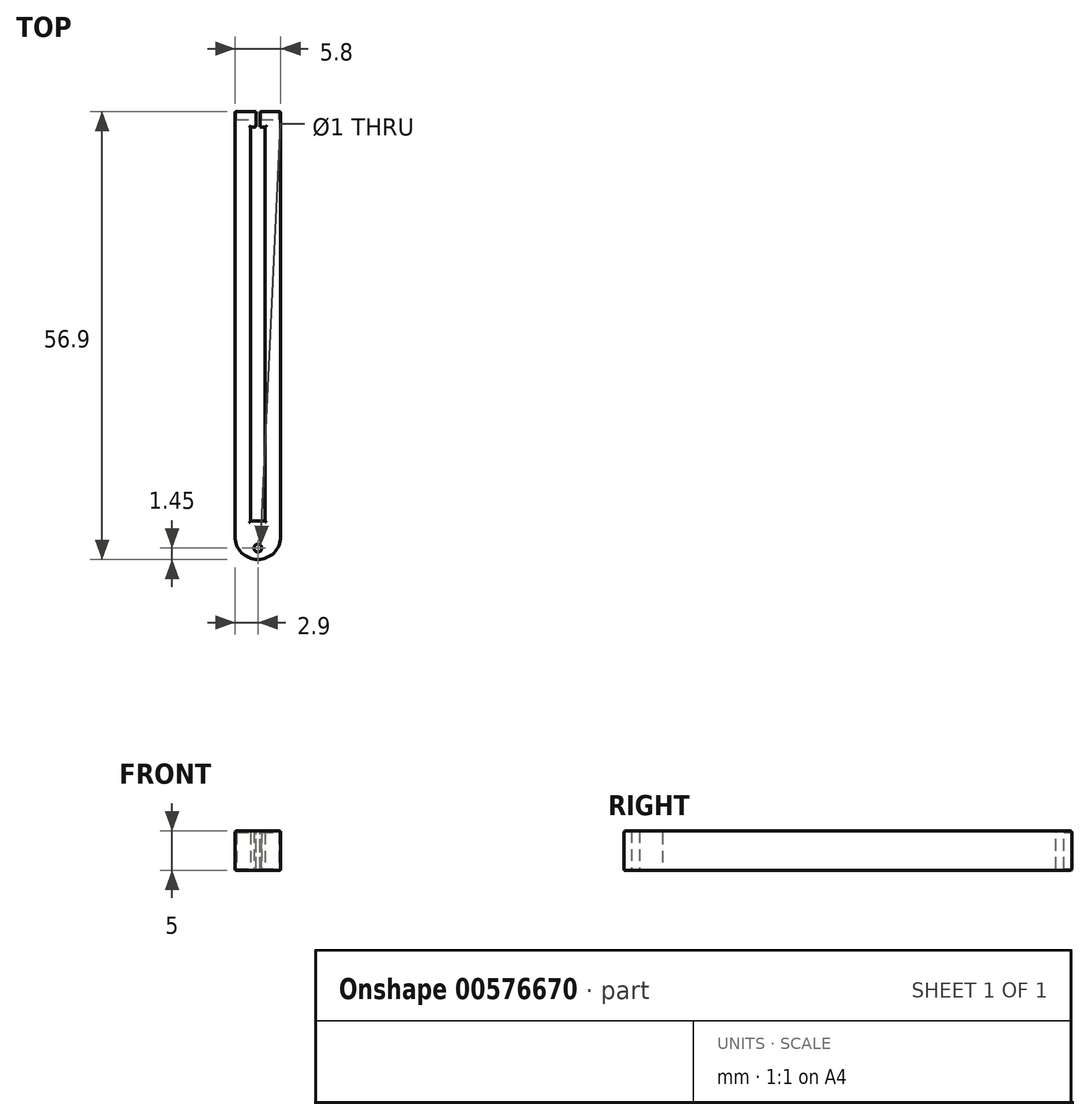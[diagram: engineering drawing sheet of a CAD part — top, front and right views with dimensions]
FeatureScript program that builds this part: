
annotation { "Feature Type Name" : "Feature", "Feature Type Description" : "" }
export const myFeature = defineFeature(function(context is Context, id is Id, definition is map)
    precondition{}
    {
        {
            var Q0;
            Q0=qCreatedBy(makeId("Top.planeOp"),FACE);
            var sketch = newSketch(context, id + "F0", { "sketchPlane" : qUnion([Q0])});
            skLineSegment(sketch, "E0", {"start": v(0, 0) * mm, "end": v(0, 50) * mm});
            skLineSegment(sketch, "E1", {"start": v(0, 50) * mm, "end": v(-1.8, 50) * mm});
            skLineSegment(sketch, "E2", {"start": v(-1.8, 50) * mm, "end": v(-1.8, 0) * mm});
            skLineSegment(sketch, "E3", {"start": v(-1.8, 0) * mm, "end": v(0, 0) * mm});
            skLineSegment(sketch, "E4", {"start": v(2, 52) * mm, "end": v(2, -2) * mm});
            skLineSegment(sketch, "E5", {"start": v(2, -2) * mm, "end": v(-3.8, -2) * mm});
            skLineSegment(sketch, "E6", {"start": v(-3.8, -2) * mm, "end": v(-3.8, 52) * mm});
            skLineSegment(sketch, "E7", {"start": v(-3.8, 52) * mm, "end": v(2, 52) * mm});
            skLineSegment(sketch, "E8", {"start": v(-0.9, -2) * mm, "end": v(-0.9, -4.9) * mm});
            skArc(sketch, "E9", {"start": v(-3.8, -2) * mm, "mid": v(-0.9, -4.9) * mm, "end": v(2, -2) * mm});
            skCircle(sketch, "E10", {"center": v(-0.9, -3.45) * mm, "radius": 0.5 * mm});
            skSolve(sketch);
        }
        {
            var Q0;
            Q0=makeQuery(id+"F0.imprint","IMPRINT",FACE,{"disambiguationData":[TD([[makeQuery(id+"F0.imprint","IMPRINT",EDGE,{"derivedFrom":sQuery(id+"F0.wireOp",EDGE,"E0")}),-1.0]])]});
            var Q1;
            {var subQ1=sQuery(id+"F0.wireOp",EDGE,"E5");var subQ3=sQuery(id+"F0.wireOp",EDGE,"E8");var subQ7=makeQuery(id+"F0.imprint","INTERSECT",VERTEX,{"derivedFrom":[subQ1,subQ3]});Q1=makeQuery(id+"F0.imprint","IMPRINT",FACE,{"disambiguationData":[TD([[makeQuery(id+"F0.imprint","IMPRINT",EDGE,{"disambiguationData":[TD([[subQ7,-1.0]])],"derivedFrom":subQ3}),1.0]])]});}
            var Q2;
            {var subQ1=sQuery(id+"F0.wireOp",EDGE,"E5");var subQ3=sQuery(id+"F0.wireOp",EDGE,"E8");var subQ5=makeQuery(id+"F0.imprint","INTERSECT",VERTEX,{"derivedFrom":[subQ1,subQ3]});Q2=makeQuery(id+"F0.imprint","IMPRINT",FACE,{"disambiguationData":[TD([[makeQuery(id+"F0.imprint","IMPRINT",EDGE,{"disambiguationData":[TD([[subQ5,-1.0]])],"derivedFrom":subQ3}),-1.0]])]});}
            extrude(context, id + "F1", {"entities" : qUnion([Q0, Q1, Q2]), "depth" : 5 * mm, "offsetDistance" : 25 * mm});
        }
        {
            var Q0;
            Q0=makeQuery(id+"F1.opExtrude","SWEPT_FACE",FACE,{"disambiguationData":[OSD([sQuery(id+"F0.wireOp",EDGE,"E7")])]});
            var sketch = newSketch(context, id + "F2", { "sketchPlane" : qUnion([Q0])});
            skLineSegment(sketch, "E11", {"start": v(0.65, 0) * mm, "end": v(0.65, 5) * mm});
            skLineSegment(sketch, "E12", {"start": v(1.15, 0) * mm, "end": v(1.15, 5) * mm});
            skLineSegment(sketch, "E13", {"start": v(1.15, 5) * mm, "end": v(0.65, 5) * mm});
            skLineSegment(sketch, "E14", {"start": v(1.15, 0) * mm, "end": v(0.65, 0) * mm});
            skSolve(sketch);
        }
        {
            var Q0;
            Q0=makeQuery(id+"F2.imprint","IMPRINT",FACE,{"disambiguationData":[TD([[makeQuery(id+"F2.imprint","IMPRINT",EDGE,{"derivedFrom":sQuery(id+"F2.wireOp",EDGE,"E11")}),-1.0]])]});
            extrude(context, id + "F3", {"entities" : qUnion([Q0]), "operationType" : NewBodyOperationType.REMOVE, "oppositeDirection" : true, "depth" : 2 * mm, "offsetDistance" : 25 * mm});
        }
        {
            var Q0;
            Q0=makeQuery(id+"F1.opExtrude","SWEPT_EDGE",EDGE,{"disambiguationData":[OSD([sQuery(id+"F0.wireOp",EDGE,"E4"),sQuery(id+"F0.wireOp",EDGE,"E7")])]});
            var Q1;
            {var subQ0=sQuery(id+"F0.wireOp",EDGE,"E7");var subQ1=sQuery(id+"F0.wireOp",EDGE,"E4");Q1=makeQuery(id+"F3.boolean.opBoolean","SPLIT",EDGE,{"disambiguationData":[TD([makeQuery(id+"F1.opExtrude","SWEPT_FACE",FACE,{"disambiguationData":[OSD([subQ1])]})])],"derivedFrom":makeQuery(id+"F1.opExtrude","CAP_EDGE",EDGE,{"disambiguationData":[OSD([subQ0])],"isStart":true})});}
            var Q2;
            {var subQ0=sQuery(id+"F0.wireOp",EDGE,"E7");var subQ1=sQuery(id+"F0.wireOp",EDGE,"E4");Q2=makeQuery(id+"F3.boolean.opBoolean","SPLIT",EDGE,{"disambiguationData":[TD([makeQuery(id+"F1.opExtrude","SWEPT_FACE",FACE,{"disambiguationData":[OSD([subQ1])]})])],"derivedFrom":makeQuery(id+"F1.opExtrude","CAP_EDGE",EDGE,{"disambiguationData":[OSD([subQ0])],"isStart":false})});}
            var Q3;
            {var subQ0=sQuery(id+"F0.wireOp",EDGE,"E7");var subQ1=sQuery(id+"F0.wireOp",EDGE,"E6");Q3=makeQuery(id+"F3.boolean.opBoolean","SPLIT",EDGE,{"disambiguationData":[TD([makeQuery(id+"F1.opExtrude","SWEPT_FACE",FACE,{"disambiguationData":[OSD([subQ1])]})])],"derivedFrom":makeQuery(id+"F1.opExtrude","CAP_EDGE",EDGE,{"disambiguationData":[OSD([subQ0])],"isStart":false})});}
            var Q4;
            Q4=makeQuery(id+"F1.opExtrude","SWEPT_EDGE",EDGE,{"disambiguationData":[OSD([sQuery(id+"F0.wireOp",EDGE,"E6"),sQuery(id+"F0.wireOp",EDGE,"E7")])]});
            var Q5;
            {var subQ0=sQuery(id+"F0.wireOp",EDGE,"E7");var subQ1=sQuery(id+"F0.wireOp",EDGE,"E6");Q5=makeQuery(id+"F3.boolean.opBoolean","SPLIT",EDGE,{"disambiguationData":[TD([makeQuery(id+"F1.opExtrude","SWEPT_FACE",FACE,{"disambiguationData":[OSD([subQ1])]})])],"derivedFrom":makeQuery(id+"F1.opExtrude","CAP_EDGE",EDGE,{"disambiguationData":[OSD([subQ0])],"isStart":true})});}
            var Q6;
            Q6=makeQuery(id+"F3.boolean.opBoolean","COPY",EDGE,{"derivedFrom":makeQuery(id+"F3.opExtrude","CAP_EDGE",EDGE,{"disambiguationData":[OSD([sQuery(id+"F2.wireOp",EDGE,"E11")])],"isStart":true})});
            var Q7;
            Q7=makeQuery(id+"F3.boolean.opBoolean","COPY",EDGE,{"derivedFrom":makeQuery(id+"F3.opExtrude","CAP_EDGE",EDGE,{"disambiguationData":[OSD([sQuery(id+"F2.wireOp",EDGE,"E12")])],"isStart":true})});
            var Q8;
            Q8=makeQuery(id+"F3.boolean.opBoolean","COPY",EDGE,{"derivedFrom":makeQuery(id+"F3.opExtrude","SWEPT_EDGE",EDGE,{"disambiguationData":[OSD([sQuery(id+"F0.wireOp",EDGE,"E7"),sQuery(id+"F2.wireOp",EDGE,"E12"),sQuery(id+"F2.wireOp",EDGE,"E13")])]})});
            var Q9;
            Q9=makeQuery(id+"F3.boolean.opBoolean","COPY",EDGE,{"derivedFrom":makeQuery(id+"F3.opExtrude","SWEPT_EDGE",EDGE,{"disambiguationData":[OSD([sQuery(id+"F0.wireOp",EDGE,"E7"),sQuery(id+"F2.wireOp",EDGE,"E11"),sQuery(id+"F2.wireOp",EDGE,"E13")])]})});
            var Q10;
            Q10=makeQuery(id+"F3.boolean.opBoolean","COPY",EDGE,{"derivedFrom":makeQuery(id+"F3.opExtrude","SWEPT_EDGE",EDGE,{"disambiguationData":[OSD([sQuery(id+"F0.wireOp",EDGE,"E7"),sQuery(id+"F2.wireOp",EDGE,"E11"),sQuery(id+"F2.wireOp",EDGE,"E14")])]})});
            var Q11;
            Q11=makeQuery(id+"F3.boolean.opBoolean","COPY",EDGE,{"derivedFrom":makeQuery(id+"F3.opExtrude","SWEPT_EDGE",EDGE,{"disambiguationData":[OSD([sQuery(id+"F0.wireOp",EDGE,"E7"),sQuery(id+"F2.wireOp",EDGE,"E12"),sQuery(id+"F2.wireOp",EDGE,"E14")])]})});
            var Q12;
            {var subQ0=sQuery(id+"F0.wireOp",EDGE,"E2");var subQ1=sQuery(id+"F0.wireOp",EDGE,"E1");Q12=makeQuery(id+"F3.boolean.opBoolean","SPLIT",EDGE,{"disambiguationData":[TD([makeQuery(id+"F1.opExtrude","SWEPT_FACE",FACE,{"disambiguationData":[OSD([subQ0])]})])],"derivedFrom":makeQuery(id+"F1.opExtrude","CAP_EDGE",EDGE,{"disambiguationData":[OSD([subQ1])],"isStart":true})});}
            var Q13;
            Q13=makeQuery(id+"F3.boolean.opBoolean","COPY",EDGE,{"derivedFrom":makeQuery(id+"F3.opExtrude","CAP_EDGE",EDGE,{"disambiguationData":[OSD([sQuery(id+"F2.wireOp",EDGE,"E12")])],"isStart":false})});
            var Q14;
            {var subQ0=sQuery(id+"F0.wireOp",EDGE,"E0");var subQ1=sQuery(id+"F0.wireOp",EDGE,"E1");Q14=makeQuery(id+"F3.boolean.opBoolean","SPLIT",EDGE,{"disambiguationData":[TD([makeQuery(id+"F1.opExtrude","SWEPT_FACE",FACE,{"disambiguationData":[OSD([subQ0])]})])],"derivedFrom":makeQuery(id+"F1.opExtrude","CAP_EDGE",EDGE,{"disambiguationData":[OSD([subQ1])],"isStart":true})});}
            var Q15;
            Q15=makeQuery(id+"F3.boolean.opBoolean","COPY",EDGE,{"derivedFrom":makeQuery(id+"F3.opExtrude","CAP_EDGE",EDGE,{"disambiguationData":[OSD([sQuery(id+"F2.wireOp",EDGE,"E11")])],"isStart":false})});
            var Q16;
            {var subQ0=sQuery(id+"F0.wireOp",EDGE,"E2");var subQ1=sQuery(id+"F0.wireOp",EDGE,"E1");Q16=makeQuery(id+"F3.boolean.opBoolean","SPLIT",EDGE,{"disambiguationData":[TD([makeQuery(id+"F1.opExtrude","SWEPT_FACE",FACE,{"disambiguationData":[OSD([subQ0])]})])],"derivedFrom":makeQuery(id+"F1.opExtrude","CAP_EDGE",EDGE,{"disambiguationData":[OSD([subQ1])],"isStart":false})});}
            var Q17;
            {var subQ0=sQuery(id+"F0.wireOp",EDGE,"E0");var subQ1=sQuery(id+"F0.wireOp",EDGE,"E1");Q17=makeQuery(id+"F3.boolean.opBoolean","SPLIT",EDGE,{"disambiguationData":[TD([makeQuery(id+"F1.opExtrude","SWEPT_FACE",FACE,{"disambiguationData":[OSD([subQ0])]})])],"derivedFrom":makeQuery(id+"F1.opExtrude","CAP_EDGE",EDGE,{"disambiguationData":[OSD([subQ1])],"isStart":false})});}
            var Q18;
            Q18=makeQuery(id+"F1.opExtrude","CAP_EDGE",EDGE,{"disambiguationData":[OSD([sQuery(id+"F0.wireOp",EDGE,"E4")])],"isStart":false});
            var Q19;
            Q19=makeQuery(id+"F1.opExtrude","CAP_EDGE",EDGE,{"disambiguationData":[OSD([sQuery(id+"F0.wireOp",EDGE,"E4")])],"isStart":true});
            var Q20;
            Q20=makeQuery(id+"F1.opExtrude","CAP_EDGE",EDGE,{"disambiguationData":[OSD([sQuery(id+"F0.wireOp",EDGE,"E2")])],"isStart":false});
            var Q21;
            Q21=makeQuery(id+"F1.opExtrude","CAP_EDGE",EDGE,{"disambiguationData":[OSD([sQuery(id+"F0.wireOp",EDGE,"E2")])],"isStart":true});
            var Q22;
            Q22=makeQuery(id+"F1.opExtrude","CAP_EDGE",EDGE,{"disambiguationData":[OSD([sQuery(id+"F0.wireOp",EDGE,"E0")])],"isStart":false});
            var Q23;
            Q23=makeQuery(id+"F1.opExtrude","CAP_EDGE",EDGE,{"disambiguationData":[OSD([sQuery(id+"F0.wireOp",EDGE,"E0")])],"isStart":true});
            var Q24;
            Q24=makeQuery(id+"F1.opExtrude","CAP_EDGE",EDGE,{"disambiguationData":[OSD([sQuery(id+"F0.wireOp",EDGE,"E3")])],"isStart":true});
            var Q25;
            Q25=makeQuery(id+"F1.opExtrude","CAP_EDGE",EDGE,{"disambiguationData":[OSD([sQuery(id+"F0.wireOp",EDGE,"E3")])],"isStart":false});
            fillet(context, id + "F4", {"entities" : qUnion([Q0, Q1, Q2, Q3, Q4, Q5, Q6, Q7, Q8, Q9, Q10, Q11, Q12, Q13, Q14, Q15, Q16, Q17, Q18, Q19, Q20, Q21, Q22, Q23, Q24, Q25]), "radius" : .2 * mm, "tangentPropagation" : true, "allowEdgeOverflow" : false});
        }
        {
            var Q0;
            {var subQ2=sQuery(id+"F0.wireOp",EDGE,"E7");var subQ3=sQuery(id+"F0.wireOp",EDGE,"E6");Q0=makeQuery(id+"F3.boolean.opBoolean","SPLIT",FACE,{"disambiguationData":[TD([makeQuery(id+"F1.opExtrude","SWEPT_FACE",FACE,{"disambiguationData":[OSD([subQ3])]})])],"derivedFrom":makeQuery(id+"F1.opExtrude","SWEPT_FACE",FACE,{"disambiguationData":[OSD([subQ2])]})});}
            var Q1;
            {var subQ2=sQuery(id+"F0.wireOp",EDGE,"E7");var subQ4=sQuery(id+"F0.wireOp",EDGE,"E4");Q1=makeQuery(id+"F3.boolean.opBoolean","SPLIT",FACE,{"disambiguationData":[TD([makeQuery(id+"F1.opExtrude","SWEPT_FACE",FACE,{"disambiguationData":[OSD([subQ4])]})])],"derivedFrom":makeQuery(id+"F1.opExtrude","SWEPT_FACE",FACE,{"disambiguationData":[OSD([subQ2])]})});}
            extrude(context, id + "F5", {"entities" : qUnion([Q0, Q1]), "operationType" : NewBodyOperationType.REMOVE, "oppositeDirection" : true, "depth" : 1 * mm, "offsetDistance" : 25 * mm});
        }
    });
